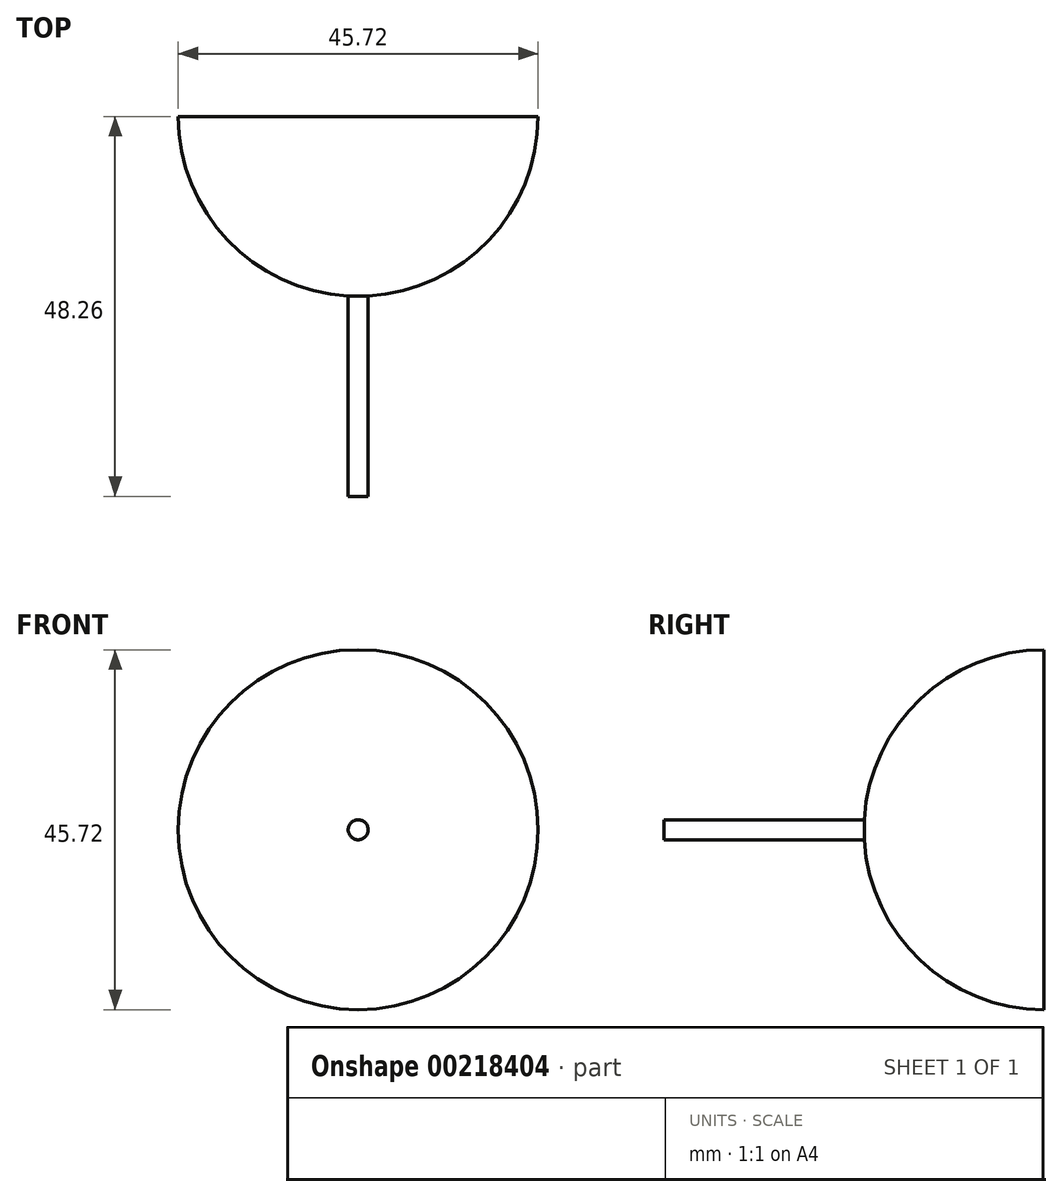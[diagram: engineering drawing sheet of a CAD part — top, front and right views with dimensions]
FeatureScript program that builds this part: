
annotation { "Feature Type Name" : "Feature", "Feature Type Description" : "" }
export const myFeature = defineFeature(function(context is Context, id is Id, definition is map)
    precondition{}
    {
        {
            var Q0;
            Q0=qCreatedBy(makeId("Front.planeOp"),FACE);
            var sketch = newSketch(context, id + "F0", { "sketchPlane" : qUnion([Q0])});
            skArc(sketch, "E0", {"start": v(0, -22.86) * mm, "mid": v(22.86, 0) * mm, "end": v(0, 22.86) * mm});
            skLineSegment(sketch, "E1", {"start": v(0, 22.86) * mm, "end": v(0, -22.86) * mm});
            skSolve(sketch);
        }
        {
            var Q0;
            Q0 = qSketchRegion(id + "F0", true);
            var Q1;
            Q1=sQuery(id+"F0.wireOp",EDGE,"E1");
            revolve(context, id + "F1", {"entities" : qUnion([Q0]), "axis" : qUnion([Q1]), "revolveType" : RevolveType.FULL});
        }
        {
            var Q0;
            Q0=qCreatedBy(makeId("Front.planeOp"),FACE);
            var sketch = newSketch(context, id + "F2", { "sketchPlane" : qUnion([Q0])});
            skCircle(sketch, "E2", {"center": v(0, 0) * mm, "radius": 1.27 * mm});
            skSolve(sketch);
        }
        {
            var Q0;
            Q0 = qSketchRegion(id + "F2", true);
            extrude(context, id + "F3", {"entities" : qUnion([Q0]), "operationType" : NewBodyOperationType.ADD, "depth" : 48.26 * mm, "hasSecondDirection" : true, "secondDirectionOppositeDirection" : true, "secondDirectionDepth" : 48.26 * mm});
        }
        {
            var Q0;
            Q0=qCreatedBy(makeId("Front.planeOp"),FACE);
            var sketch = newSketch(context, id + "F4", { "sketchPlane" : qUnion([Q0])});
            skCircle(sketch, "E3", {"center": v(0, 0) * mm, "radius": 26.18 * mm});
            skSolve(sketch);
        }
        {
            var Q0;
            Q0 = qSketchRegion(id + "F4", true);
            extrude(context, id + "F5", {"entities" : qUnion([Q0]), "operationType" : NewBodyOperationType.REMOVE, "endBound" : BoundingType.THROUGH_ALL, "oppositeDirection" : true, "depth" : 25.4 * mm});
        }
    });
